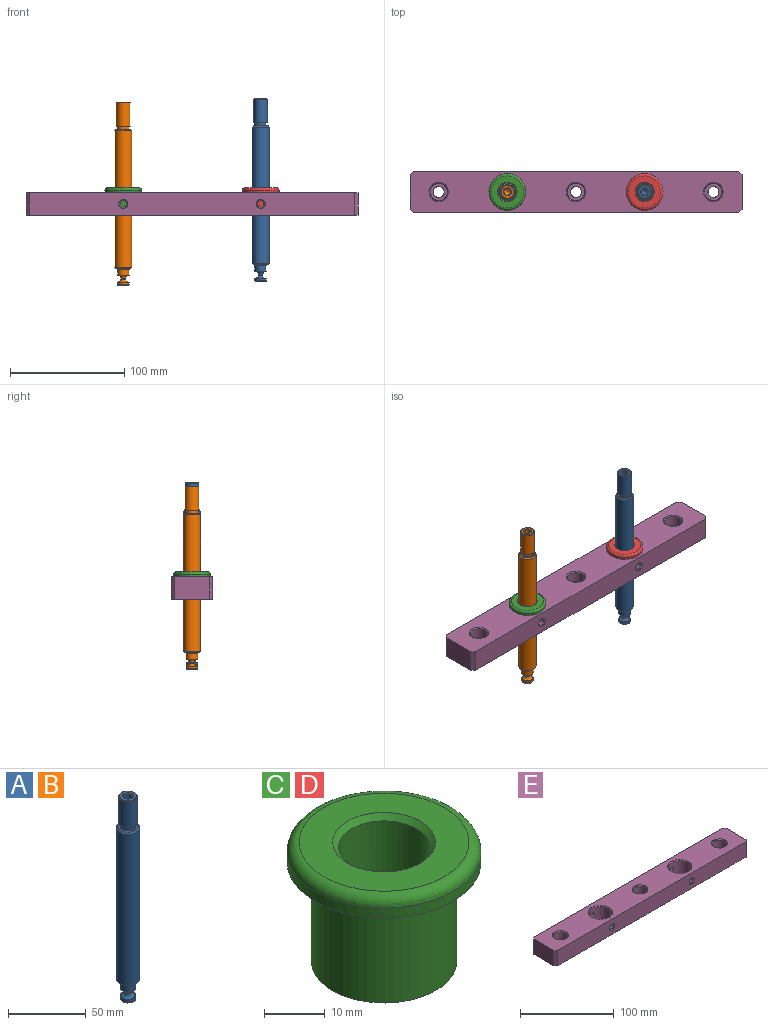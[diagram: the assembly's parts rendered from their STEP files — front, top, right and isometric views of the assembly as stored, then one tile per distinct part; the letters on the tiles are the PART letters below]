
ASSEMBLY  parts=5 mates=6
PART A: 23 faces, bbox 15x15x160 mm
  f0: cylinder r=5mm len=10mm, axis (0,0,-1), area 157.1mm2, adj f12,f17
  f1: plane 13x13mm, normal (0,0,-1), area 19.6mm2, adj f13,f17
  f2: cylinder r=7.5mm len=119mm, axis (0,0,-1), area 5607.7mm2, adj f13,f14
  f3: plane 13x13mm, normal (0,0,1), area 54.2mm2, adj f4,f14
  f4: cylinder r=5mm len=10mm, axis (0,0,-1), area 94.2mm2, adj f3,f5
  f5: plane 12x12mm, normal (0,0,-1), area 34.6mm2, adj f4,f6
  f6: cylinder r=6mm len=20.5mm, axis (0,0,-1), area 772.8mm2, adj f5,f19
  f7: plane 11x11mm, normal (0,0,1), area 56.5mm2, adj f19,f22
  f8: plane 8x8mm, normal (0,0,-1), area 50.3mm2, adj f18
  f9: cylinder r=5mm len=10mm, axis (0,0,-1), area 62.8mm2, adj f10,f18
  f10: plane 10x10mm, normal (0,0,1), area 14.9mm2, adj f9,f15
  f11: cylinder r=2mm len=4mm, axis (0,0,-1), area 12.6mm2, adj f15,f16
  f12: plane 10x10mm, normal (0,0,-1), area 14.9mm2, adj f0,f16
  f13: cone r=6.5mm half-angle=45deg, axis (0,0,1), area 62.2mm2, adj f1,f2
  f14: cone r=7.5mm half-angle=45deg, axis (0,0,-1), area 62.2mm2, adj f2,f3
  f15: torus R=4.5mm, axis (0,0,-1), area 71.8mm2, adj f10,f11
  f16: torus R=4.5mm, axis (0,0,1), area 71.8mm2, adj f11,f12
  f17: torus R=6mm, axis (0,0,1), area 52.9mm2, adj f0,f1
  f18: torus R=4mm, axis (0,0,-1), area 45.8mm2, adj f8,f9
  f19: cone r=6mm half-angle=45deg, axis (0,0,-1), area 25.5mm2, adj f6,f7
  f20: cone r=0mm half-angle=59deg, axis (0,0,1), area 33mm2, adj f21
  f21: cylinder r=3mm len=19.5mm, axis (0,0,1), area 367.6mm2, adj f20,f22
  f22: cone r=3mm half-angle=45deg, axis (0,0,1), area 14.4mm2, adj f7,f21
PART B: same geometry as A
PART C: 8 faces, bbox 34.6x34.6x24 mm
  f0: cylinder r=7.5mm len=23mm, axis (0,0,1), area 1083.8mm2, adj f1,f6
  f1: plane 24x24mm, normal (0,0,-1), area 275.7mm2, adj f0,f2
  f2: cylinder r=12mm len=24mm, axis (0,0,1), area 1508mm2, adj f1,f3
  f3: plane 32x32mm, normal (0,0,-1), area 351.9mm2, adj f2,f4
  f4: cylinder r=16mm len=32mm, axis (0,0,1), area 201.1mm2, adj f3,f7
  f5: plane 28x28mm, normal (0,0,1), area 388.8mm2, adj f6,f7
  f6: cone r=7.5mm half-angle=45deg, axis (0,0,1), area 71.1mm2, adj f0,f5
  f7: torus R=14mm, axis (0,0,-1), area 301.5mm2, adj f4,f5
PART D: same geometry as C
PART E: 34 faces, bbox 290x36x20 mm
  f0: cylinder r=12mm len=24mm, axis (0,0,1), area 1375.7mm2, adj f6,f17,f24,f25
  f1: cylinder r=12mm len=24mm, axis (0,0,1), area 1375.7mm2, adj f6,f18,f22,f23
  f2: cylinder r=4.75mm len=10mm, axis (0,0,1), area 298.5mm2, adj f6,f16
  f3: cylinder r=4.75mm len=10mm, axis (0,0,1), area 298.5mm2, adj f6,f14
  f4: cylinder r=4.75mm len=10mm, axis (0,0,1), area 298.5mm2, adj f6,f12
  f5: plane 30x20mm, normal (-1,0,0), area 600mm2, adj f6,f8,f30,f33
  f6: plane 290x36mm, normal (0,0,-1), area 9304.6mm2, adj f0,f1,f2,f3,f4,f5,f7,f9
  f7: plane 30x20mm, normal (1,0,0), area 600mm2, adj f6,f8,f31,f32
  f8: plane 290x36mm, normal (0,0,1), area 8679.2mm2, adj f5,f7,f9,f10,f17,f18,f19,f20
  f9: plane 284x20mm, normal (0,1,0), area 5579.5mm2, adj f6,f8,f26,f28,f30,f31
  f10: plane 284x20mm, normal (0,-1,0), area 5579.5mm2, adj f6,f8,f27,f29,f32,f33
  f11: cylinder r=7.5mm len=15mm, axis (0,0,1), area 424.1mm2, adj f12,f21
  f12: plane 15x15mm, normal (0,0,1), area 105.8mm2, adj f4,f11
  f13: cylinder r=7.5mm len=15mm, axis (0,0,1), area 424.1mm2, adj f14,f20
  f14: plane 15x15mm, normal (0,0,1), area 105.8mm2, adj f3,f13
  f15: cylinder r=7.5mm len=15mm, axis (0,0,1), area 424.1mm2, adj f16,f19
  f16: plane 15x15mm, normal (0,0,1), area 105.8mm2, adj f2,f15
  f17: cone r=12mm half-angle=45deg, axis (0,0,1), area 111.1mm2, adj f0,f8
  f18: cone r=12mm half-angle=45deg, axis (0,0,1), area 111.1mm2, adj f1,f8
  f19: cone r=7.5mm half-angle=45deg, axis (0,0,1), area 71.1mm2, adj f8,f15
  f20: cone r=7.5mm half-angle=45deg, axis (0,0,1), area 71.1mm2, adj f8,f13
  f21: cone r=7.5mm half-angle=45deg, axis (0,0,1), area 71.1mm2, adj f8,f11
  f22: cylinder r=3mm len=6mm, axis (0,-1,0), area 97.8mm2, adj f1,f29
  f23: cylinder r=3mm len=6mm, axis (0,-1,0), area 97.8mm2, adj f1,f28
  f24: cylinder r=3mm len=6mm, axis (0,-1,0), area 97.8mm2, adj f0,f27
  f25: cylinder r=3mm len=6mm, axis (0,-1,0), area 97.8mm2, adj f0,f26
  f26: cone r=3mm half-angle=45deg, axis (0,1,0), area 31.1mm2, adj f9,f25
  f27: cone r=3mm half-angle=45deg, axis (0,-1,0), area 31.1mm2, adj f10,f24
  f28: cone r=3mm half-angle=45deg, axis (0,1,0), area 31.1mm2, adj f9,f23
  f29: cone r=3mm half-angle=45deg, axis (0,-1,0), area 31.1mm2, adj f10,f22
  f30: plane 20x3mm, normal (-0.71,0.71,0), area 84.9mm2, adj f5,f6,f8,f9
  f31: plane 20x3mm, normal (0.71,0.71,0), area 84.9mm2, adj f6,f7,f8,f9
  f32: plane 20x3mm, normal (0.71,-0.71,0), area 84.9mm2, adj f6,f7,f8,f10
  f33: plane 20x3mm, normal (-0.71,-0.71,0), area 84.9mm2, adj f5,f6,f8,f10
PLACE A t=(145.89,109.46,-150.05)mm
PLACE B t=(25.89,109.46,-153.4)mm
PLACE C t=(25.89,109.46,-92.17)mm
PLACE D t=(145.89,109.46,-92.17)mm
PLACE E t=(-59.11,91.46,-92.17)mm
MATE slider D.f0 <-> A.f0  axis (0,0,1) through (145.89,109.46,-69.17)mm
MATE cylindrical E.f0 <-> D.f0  axis (0,0,1) through (145.89,109.46,-73.17)mm
MATE cylindrical E.f1 <-> C.f0  axis (0,0,1) through (25.89,109.46,-73.17)mm
MATE planar C.f0 <-> E.f3  axis (0,0,-1) through (25.89,109.46,-72.17)mm
MATE planar D.f0 <-> E.f3  axis (0,0,-1) through (145.89,109.46,-72.17)mm
MATE slider C.f0 <-> B.f0  axis (0,0,1) through (25.89,109.46,-69.17)mm
